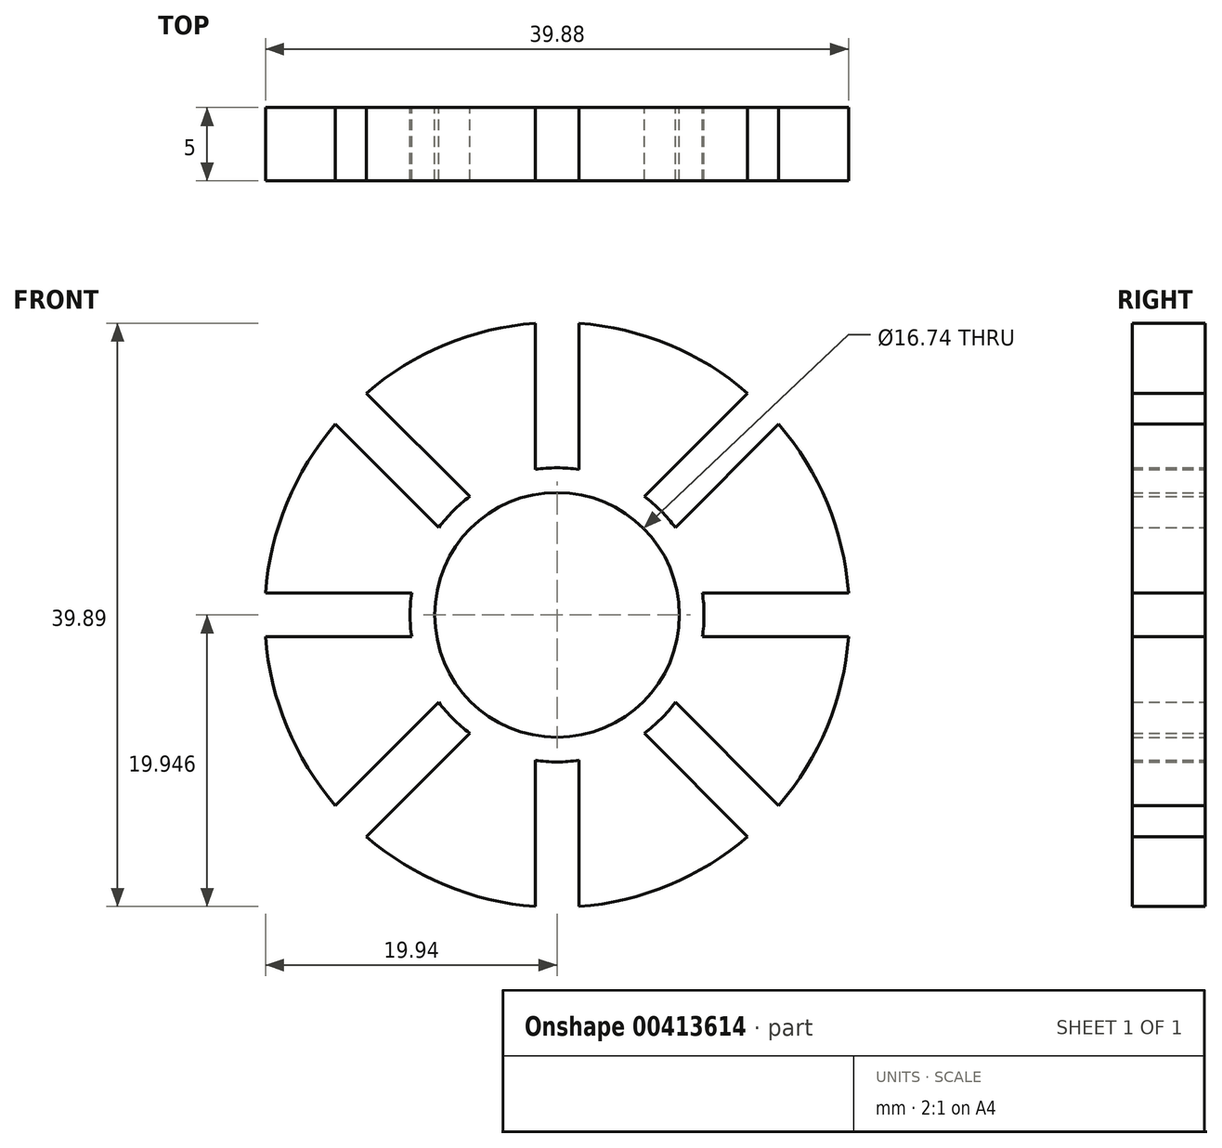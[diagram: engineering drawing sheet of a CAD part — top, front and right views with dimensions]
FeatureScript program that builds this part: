
annotation { "Feature Type Name" : "Feature", "Feature Type Description" : "" }
export const myFeature = defineFeature(function(context is Context, id is Id, definition is map)
    precondition{}
    {
        {
            var Q0;
            Q0=qCreatedBy(makeId("Front.planeOp"),FACE);
            var sketch = newSketch(context, id + "F0", { "sketchPlane" : qUnion([Q0])});
            skLineSegment(sketch, "E0", {"start": v(0, 0) * mm, "end": v(-3, 0) * mm});
            skLineSegment(sketch, "E1", {"start": v(-3, 0) * mm, "end": v(-3, 10) * mm});
            skLineSegment(sketch, "E2", {"start": v(0, 10) * mm, "end": v(0, 0) * mm});
            skArc(sketch, "E3", {"start": v(-3, 10) * mm, "mid": v(-9.15, 8.53) * mm, "end": v(-14.54, 5.22) * mm});
            skLineSegment(sketch, "E4.1.0", {"start": v(-14.54, 5.22) * mm, "end": v(-7.47, -1.85) * mm});
            skLineSegment(sketch, "E4.1.2", {"start": v(-9.6, -3.97) * mm, "end": v(-16.66, 3.1) * mm});
            skLineSegment(sketch, "E4.1.3", {"start": v(-7.47, -1.85) * mm, "end": v(-9.6, -3.97) * mm});
            skLineSegment(sketch, "E4.2.0", {"start": v(-21.44, -8.44) * mm, "end": v(-11.44, -8.44) * mm});
            skLineSegment(sketch, "E4.2.2", {"start": v(-11.44, -11.44) * mm, "end": v(-21.44, -11.44) * mm});
            skLineSegment(sketch, "E4.2.3", {"start": v(-11.44, -8.44) * mm, "end": v(-11.44, -11.44) * mm});
            skLineSegment(sketch, "E4.3.0", {"start": v(-16.66, -22.99) * mm, "end": v(-9.6, -15.91) * mm});
            skLineSegment(sketch, "E4.3.2", {"start": v(-7.47, -18.04) * mm, "end": v(-14.54, -25.1) * mm});
            skLineSegment(sketch, "E4.3.3", {"start": v(-9.6, -15.91) * mm, "end": v(-7.47, -18.04) * mm});
            skLineSegment(sketch, "E4.4.0", {"start": v(-3, -29.89) * mm, "end": v(-3, -19.89) * mm});
            skLineSegment(sketch, "E4.4.2", {"start": v(0, -19.89) * mm, "end": v(0, -29.89) * mm});
            skLineSegment(sketch, "E4.4.3", {"start": v(-3, -19.89) * mm, "end": v(0, -19.89) * mm});
            skLineSegment(sketch, "E4.5.0", {"start": v(11.54, -25.1) * mm, "end": v(4.47, -18.04) * mm});
            skLineSegment(sketch, "E4.5.2", {"start": v(6.6, -15.91) * mm, "end": v(13.66, -22.99) * mm});
            skLineSegment(sketch, "E4.5.3", {"start": v(4.47, -18.04) * mm, "end": v(6.6, -15.91) * mm});
            skLineSegment(sketch, "E4.6.0", {"start": v(18.44, -11.44) * mm, "end": v(8.44, -11.44) * mm});
            skLineSegment(sketch, "E4.6.2", {"start": v(8.44, -8.44) * mm, "end": v(18.44, -8.44) * mm});
            skLineSegment(sketch, "E4.6.3", {"start": v(8.44, -11.44) * mm, "end": v(8.44, -8.44) * mm});
            skLineSegment(sketch, "E4.7.0", {"start": v(13.66, 3.1) * mm, "end": v(6.6, -3.97) * mm});
            skLineSegment(sketch, "E4.7.2", {"start": v(4.47, -1.85) * mm, "end": v(11.54, 5.22) * mm});
            skLineSegment(sketch, "E4.7.3", {"start": v(6.6, -3.97) * mm, "end": v(4.47, -1.85) * mm});
            skArc(sketch, "E5.trimOffspring", {"start": v(-16.66, 3.1) * mm, "mid": v(-19.98, -2.3) * mm, "end": v(-21.44, -8.44) * mm});
            skArc(sketch, "E6.trimOffspring", {"start": v(-21.44, -11.44) * mm, "mid": v(-19.98, -17.6) * mm, "end": v(-16.66, -22.99) * mm});
            skArc(sketch, "E7.trimOffspring", {"start": v(-14.54, -25.1) * mm, "mid": v(-9.15, -28.42) * mm, "end": v(-3, -29.89) * mm});
            skArc(sketch, "E8.trimOffspring", {"start": v(0, -29.89) * mm, "mid": v(6.15, -28.42) * mm, "end": v(11.54, -25.1) * mm});
            skArc(sketch, "E9.trimOffspring", {"start": v(13.66, -22.99) * mm, "mid": v(16.98, -17.6) * mm, "end": v(18.44, -11.44) * mm});
            skArc(sketch, "E10.trimOffspring", {"start": v(18.44, -8.44) * mm, "mid": v(16.98, -2.3) * mm, "end": v(13.66, 3.1) * mm});
            skArc(sketch, "E11.trimOffspring", {"start": v(11.54, 5.22) * mm, "mid": v(6.15, 8.53) * mm, "end": v(0, 10) * mm});
            skCircle(sketch, "E12", {"center": v(-1.5, -9.94) * mm, "radius": 10.06 * mm});
            skCircle(sketch, "E13", {"center": v(-1.5, -9.94) * mm, "radius": 8.37 * mm});
            skSolve(sketch);
        }
        {
            var Q0;
            Q0 = qSketchRegion(id + "F0", true);
            extrude(context, id + "F1", {"entities" : qUnion([Q0]), "depth" : 5 * mm, "offsetDistance" : 25 * mm});
        }
        {
            var Q0;
            Q0 = qSketchRegion(id + "F0", true);
            extrude(context, id + "F2", {"entities" : qUnion([Q0]), "operationType" : NewBodyOperationType.ADD, "depth" : 5 * mm, "offsetDistance" : 25 * mm});
        }
    });
